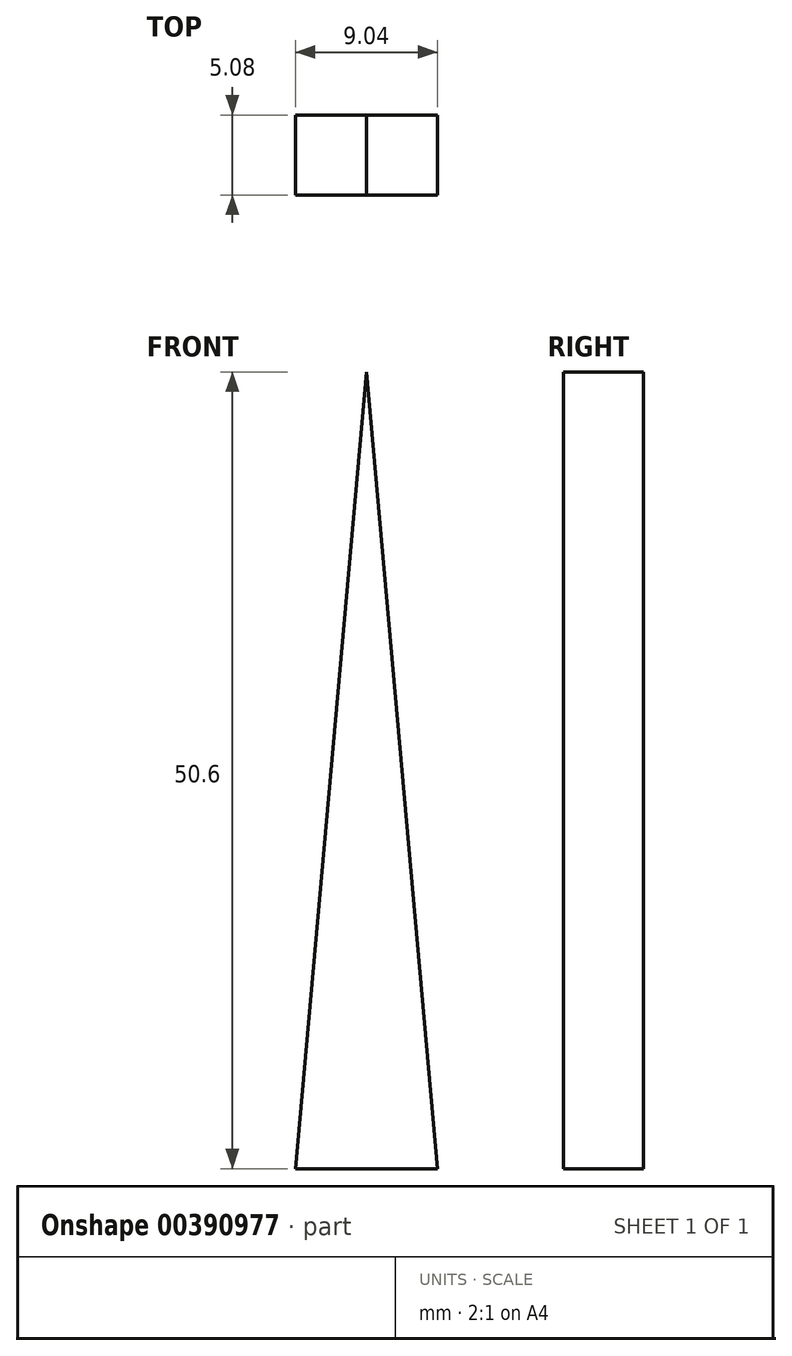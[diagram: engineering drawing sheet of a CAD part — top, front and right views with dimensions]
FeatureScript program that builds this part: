
annotation { "Feature Type Name" : "Feature", "Feature Type Description" : "" }
export const myFeature = defineFeature(function(context is Context, id is Id, definition is map)
    precondition{}
    {
        {
            var Q0;
            Q0=qCreatedBy(makeId("Front.planeOp"),FACE);
            var sketch = newSketch(context, id + "F0", { "sketchPlane" : qUnion([Q0])});
            skLineSegment(sketch, "E0", {"start": v(0, -46.98) * mm, "end": v(0, 77.1) * mm, "construction": true});
            skLineSegment(sketch, "E1", {"start": v(0, 77.1) * mm, "end": v(-4.52, 26.5) * mm});
            skLineSegment(sketch, "E2.MirrorCS", {"start": v(0, 77.1) * mm, "end": v(4.52, 26.5) * mm});
            skLineSegment(sketch, "E3", {"start": v(-4.52, 26.5) * mm, "end": v(4.52, 26.5) * mm});
            skSolve(sketch);
        }
        {
            var Q0;
            Q0=qSketchRegion(id+"F0",true);
            extrude(context, id + "F1", {"entities" : qUnion([Q0]), "endBound" : BoundingType.SYMMETRIC, "depth" : 5.08 * mm});
        }
    });
